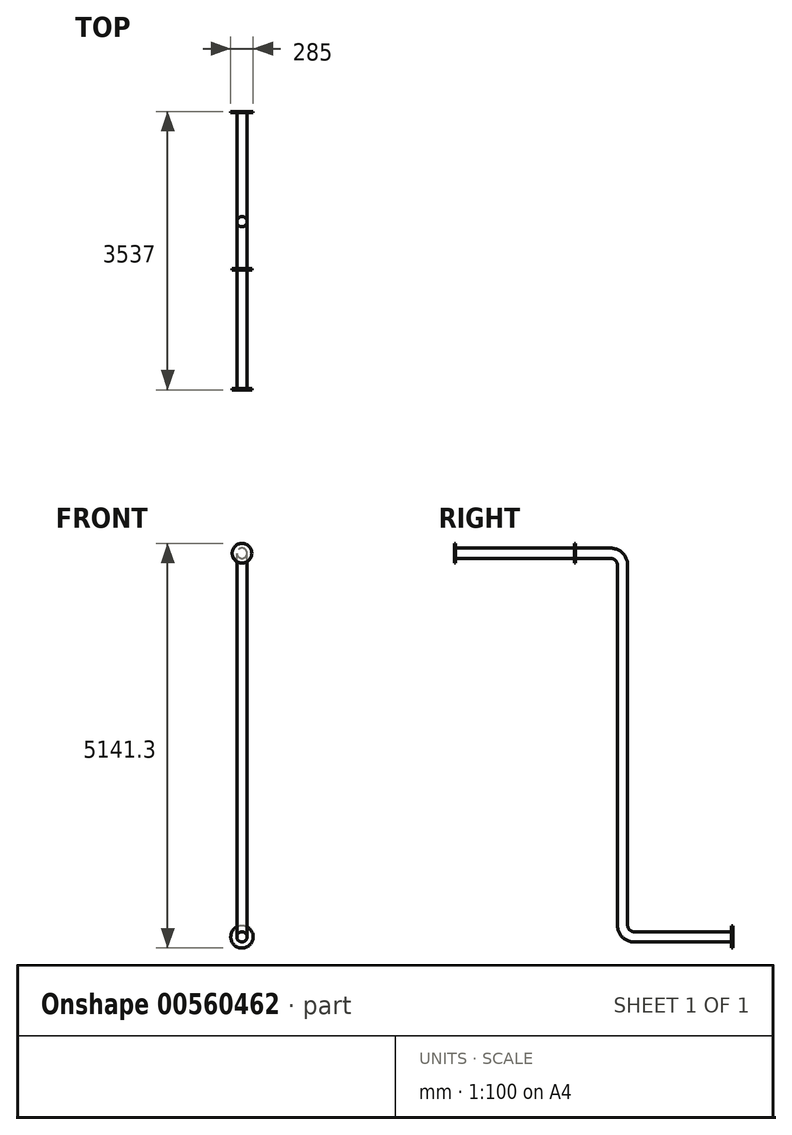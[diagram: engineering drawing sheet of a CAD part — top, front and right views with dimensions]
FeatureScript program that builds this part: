
annotation { "Feature Type Name" : "Feature", "Feature Type Description" : "" }
export const myFeature = defineFeature(function(context is Context, id is Id, definition is map)
    precondition{}
    {
        {
            var Q0;
            Q0=qCreatedBy(makeId("Front.planeOp"),FACE);
            var sketch = newSketch(context, id + "F0", { "sketchPlane" : qUnion([Q0])});
            skCircle(sketch, "E0", {"center": v(0, 0) * mm, "radius": 142.5 * mm});
            skSolve(sketch);
        }
        {
            var Q0;
            Q0=qCreatedBy(makeId("Right.planeOp"),FACE);
            var sketch = newSketch(context, id + "F1", { "sketchPlane" : qUnion([Q0])});
            skLineSegment(sketch, "E1", {"start": v(0, 0) * mm, "end": v(-1250, 0) * mm});
            skLineSegment(sketch, "E2", {"start": v(-1400, 150) * mm, "end": v(-1400, 4723.8) * mm});
            skLineSegment(sketch, "E3", {"start": v(-1550, 4873.8) * mm, "end": v(-3537, 4873.8) * mm});
            skPoint(sketch, "E4.visualSharp", {"position": v(-1400, 0) * mm});
            skArc(sketch, "E4.filletArc", {"start": v(-1400, 150) * mm, "mid": v(-1356.07, 43.93) * mm, "end": v(-1250, 0) * mm});
            skPoint(sketch, "E5.visualSharp", {"position": v(-1400, 4873.8) * mm});
            skArc(sketch, "E5.filletArc", {"start": v(-1400, 4723.8) * mm, "mid": v(-1443.93, 4829.87) * mm, "end": v(-1550, 4873.8) * mm});
            skSolve(sketch);
        }
        {
            var Q0;
            Q0=qCreatedBy(makeId("Front.planeOp"),FACE);
            var sketch = newSketch(context, id + "F2", { "sketchPlane" : qUnion([Q0])});
            skCircle(sketch, "E6", {"center": v(0, 0) * mm, "radius": 65 * mm});
            skSolve(sketch);
        }
        {
            var Q0;
            Q0=qCreatedBy(makeId("Front.planeOp"),FACE);
            cPlane(context, id + "F3", {"entities" : qUnion([Q0]), "cplaneType" : CPlaneType.OFFSET, "offset" : (1400 + 2137) * mm, "width" : 150 * mm, "height" : 150 * mm});
        }
        {
            var Q0;
            Q0=qCreatedBy(id+"F3.planeOp",FACE);
            var sketch = newSketch(context, id + "F4", { "sketchPlane" : qUnion([Q0])});
            skPoint(sketch, "E7.0", {"position": v(0, 4873.8) * mm});
            skCircle(sketch, "E8", {"center": v(0, 4873.8) * mm, "radius": 125 * mm});
            skSolve(sketch);
        }
        {
            var Q0;
            Q0=makeQuery(id+"F0.imprint","IMPRINT",FACE,{"disambiguationData":[TD([[makeQuery(id+"F0.imprint","IMPRINT",EDGE,{"derivedFrom":sQuery(id+"F0.wireOp",EDGE,"E0")}),1.0]])]});
            extrude(context, id + "F5", {"entities" : qUnion([Q0]), "depth" : 15 * mm, "offsetDistance" : 25 * mm});
        }
        {
            var Q0;
            Q0=makeQuery(id+"F2.imprint","IMPRINT",FACE,{"disambiguationData":[TD([[makeQuery(id+"F2.imprint","IMPRINT",EDGE,{"derivedFrom":sQuery(id+"F2.wireOp",EDGE,"E6")}),1.0]])]});
            var Q1;
            Q1=sQuery(id+"F1.wireOp",EDGE,"E1");
            var Q2;
            Q2=sQuery(id+"F1.wireOp",EDGE,"E4.filletArc");
            var Q3;
            Q3=sQuery(id+"F1.wireOp",EDGE,"E2");
            var Q4;
            Q4=sQuery(id+"F1.wireOp",EDGE,"E5.filletArc");
            var Q5;
            Q5=sQuery(id+"F1.wireOp",EDGE,"E3");
            sweep(context, id + "F6", {"operationType" : NewBodyOperationType.ADD, "profiles" : qUnion([Q0]), "path" : qUnion([Q1, Q2, Q3, Q4, Q5])});
        }
        {
            var Q0;
            Q0=makeQuery(id+"F4.imprint","IMPRINT",FACE,{"disambiguationData":[TD([[makeQuery(id+"F4.imprint","IMPRINT",EDGE,{"derivedFrom":sQuery(id+"F4.wireOp",EDGE,"E8")}),1.0]])]});
            extrude(context, id + "F7", {"entities" : qUnion([Q0]), "operationType" : NewBodyOperationType.ADD, "oppositeDirection" : true, "depth" : 15 * mm, "offsetDistance" : 25 * mm});
        }
        {
            var Q0;
            Q0=qCreatedBy(id+"F3.planeOp",FACE);
            cPlane(context, id + "F8", {"entities" : qUnion([Q0]), "cplaneType" : CPlaneType.OFFSET, "offset" : 1540 * mm, "oppositeDirection" : true, "width" : 150 * mm, "height" : 150 * mm});
        }
        {
            var Q0;
            Q0=qCreatedBy(id+"F8.planeOp",FACE);
            var sketch = newSketch(context, id + "F9", { "sketchPlane" : qUnion([Q0])});
            skCircle(sketch, "E9", {"center": v(0, 4873.45) * mm, "radius": 125 * mm});
            skSolve(sketch);
        }
        {
            var Q0;
            Q0=makeQuery(id+"F9.imprint","IMPRINT",FACE,{"disambiguationData":[TD([[makeQuery(id+"F9.imprint","IMPRINT",EDGE,{"derivedFrom":sQuery(id+"F9.wireOp",EDGE,"E9")}),1.0]])]});
            extrude(context, id + "F10", {"entities" : qUnion([Q0]), "operationType" : NewBodyOperationType.ADD, "depth" : 15 * mm, "offsetDistance" : 25 * mm});
        }
    });
